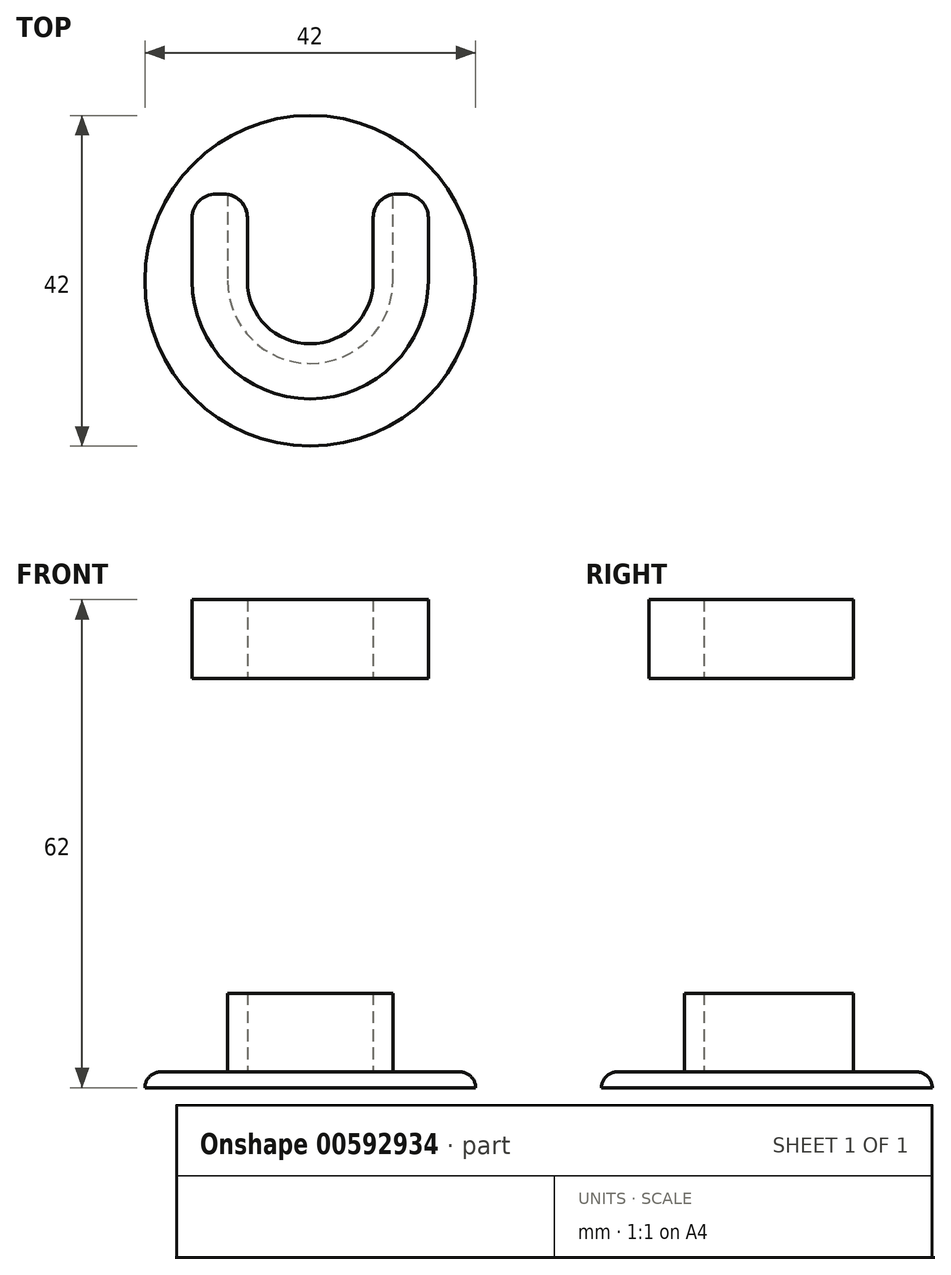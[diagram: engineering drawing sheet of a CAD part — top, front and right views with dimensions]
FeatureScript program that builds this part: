
annotation { "Feature Type Name" : "Feature", "Feature Type Description" : "" }
export const myFeature = defineFeature(function(context is Context, id is Id, definition is map)
    precondition{}
    {
        {
            var Q0;
            Q0=qCreatedBy(makeId("Top.planeOp"),FACE);
            var sketch = newSketch(context, id + "F0", { "sketchPlane" : qUnion([Q0])});
            skCircle(sketch, "E0", {"center": v(0, 0) * mm, "radius": 21 * mm});
            skCircle(sketch, "E1", {"center": v(0, 0) * mm, "radius": 8 * mm});
            skCircle(sketch, "E2", {"center": v(0, 0) * mm, "radius": 10.5 * mm});
            skLineSegment(sketch, "E3", {"start": v(-10.5, 11) * mm, "end": v(-10.5, 0) * mm});
            skLineSegment(sketch, "E4", {"start": v(-17.89, 11) * mm, "end": v(17.89, 11) * mm});
            skLineSegment(sketch, "E5", {"start": v(-8, 0) * mm, "end": v(-8, 11) * mm});
            skLineSegment(sketch, "E6", {"start": v(8, 0) * mm, "end": v(8, 11) * mm});
            skLineSegment(sketch, "E7", {"start": v(10.5, 0) * mm, "end": v(10.5, 11) * mm});
            skSolve(sketch);
        }
        {
            var Q0;
            Q0=qSketchRegion(id+"F0",true);
            var Q1;
            Q1=makeQuery(id+"F0.imprint","IMPRINT",FACE,{"disambiguationData":[TD([[makeQuery(id+"F0.imprint","IMPRINT",EDGE,{"derivedFrom":sQuery(id+"F0.wireOp",EDGE,"E1")}),1.0]])]});
            var Q2;
            Q2=makeQuery(id+"F0.imprint","IMPRINT",FACE,{"disambiguationData":[TD([[makeQuery(id+"F0.imprint","IMPRINT",EDGE,{"derivedFrom":sQuery(id+"F0.wireOp",EDGE,"E1")}),-1.0]])]});
            var Q3;
            {var subQ0=sQuery(id+"F0.wireOp",EDGE,"E2");var subQ1=makeQuery(id+"F0.imprint","IMPRINT",VERTEX,{"disambiguationData":[OD(0.0)],"derivedFrom":subQ0});Q3=makeQuery(id+"F0.imprint","IMPRINT",FACE,{"disambiguationData":[TD([[makeQuery(id+"F0.imprint","IMPRINT",EDGE,{"disambiguationData":[TD([[subQ1,-1.0]])],"derivedFrom":subQ0}),1.0]])]});}
            var Q4;
            {var subQ0=sQuery(id+"F0.wireOp",EDGE,"E3");Q4=makeQuery(id+"F0.imprint","IMPRINT",FACE,{"disambiguationData":[TD([[makeQuery(id+"F0.imprint","IMPRINT",EDGE,{"derivedFrom":subQ0}),1.0]])]});}
            var Q5;
            {var subQ0=sQuery(id+"F0.wireOp",EDGE,"E6");var subQ1=sQuery(id+"F0.wireOp",EDGE,"E2");var subQ2=makeQuery(id+"F0.imprint","INTERSECT",VERTEX,{"derivedFrom":[subQ1,subQ0]});Q5=makeQuery(id+"F0.imprint","IMPRINT",FACE,{"disambiguationData":[TD([[makeQuery(id+"F0.imprint","IMPRINT",EDGE,{"disambiguationData":[TD([[subQ2,-1.0]])],"derivedFrom":subQ1}),-1.0]])]});}
            var Q6;
            {var subQ0=sQuery(id+"F0.wireOp",EDGE,"E7");Q6=makeQuery(id+"F0.imprint","IMPRINT",FACE,{"disambiguationData":[TD([[makeQuery(id+"F0.imprint","IMPRINT",EDGE,{"derivedFrom":subQ0}),1.0]])]});}
            var Q7;
            {var subQ3=sQuery(id+"F0.wireOp",EDGE,"E5");var subQ7=sQuery(id+"F0.wireOp",EDGE,"E1");var subQ8=makeQuery(id+"F0.imprint","INTERSECT",VERTEX,{"derivedFrom":[subQ7,subQ3]});Q7=makeQuery(id+"F0.imprint","IMPRINT",FACE,{"disambiguationData":[TD([[makeQuery(id+"F0.imprint","IMPRINT",EDGE,{"disambiguationData":[TD([[subQ8,-1.0]])],"derivedFrom":subQ7}),-1.0]])]});}
            extrude(context, id + "F1", {"entities" : qUnion([Q0, Q1, Q2, Q3, Q4, Q5, Q6, Q7]), "oppositeDirection" : true, "depth" : 2 * mm, "offsetDistance" : 25 * mm});
        }
        {
            var Q0;
            {var subQ0=sQuery(id+"F0.wireOp",EDGE,"E7");Q0=makeQuery(id+"F0.imprint","IMPRINT",FACE,{"disambiguationData":[TD([[makeQuery(id+"F0.imprint","IMPRINT",EDGE,{"derivedFrom":subQ0}),1.0]])]});}
            var Q1;
            {var subQ3=sQuery(id+"F0.wireOp",EDGE,"E5");var subQ7=sQuery(id+"F0.wireOp",EDGE,"E1");var subQ8=makeQuery(id+"F0.imprint","INTERSECT",VERTEX,{"derivedFrom":[subQ7,subQ3]});Q1=makeQuery(id+"F0.imprint","IMPRINT",FACE,{"disambiguationData":[TD([[makeQuery(id+"F0.imprint","IMPRINT",EDGE,{"disambiguationData":[TD([[subQ8,-1.0]])],"derivedFrom":subQ7}),-1.0]])]});}
            var Q2;
            {var subQ0=sQuery(id+"F0.wireOp",EDGE,"E3");Q2=makeQuery(id+"F0.imprint","IMPRINT",FACE,{"disambiguationData":[TD([[makeQuery(id+"F0.imprint","IMPRINT",EDGE,{"derivedFrom":subQ0}),1.0]])]});}
            extrude(context, id + "F2", {"entities" : qUnion([Q0, Q1, Q2]), "operationType" : NewBodyOperationType.ADD, "depth" : 10 * mm, "offsetDistance" : 25 * mm});
        }
        {
            var Q0;
            Q0=makeQuery(id+"F1.opExtrude","CAP_EDGE",EDGE,{"disambiguationData":[OSD([sQuery(id+"F0.wireOp",EDGE,"E0")])],"isStart":true});
            var Q1;
            Q1=makeQuery(id+"F2.opExtrude","CAP_EDGE",EDGE,{"disambiguationData":[OSD([sQuery(id+"F0.wireOp",EDGE,"E2")])],"isStart":true});
            fillet(context, id + "F3", {"entities" : qUnion([Q0, Q1]), "radius" : 2 * mm, "tangentPropagation" : true, "allowEdgeOverflow" : false});
        }
        {
            var Q0;
            Q0=makeQuery(id+"F2.opExtrude","SWEPT_EDGE",EDGE,{"disambiguationData":[OSD([sQuery(id+"F0.wireOp",EDGE,"E4"),sQuery(id+"F0.wireOp",EDGE,"E5")])]});
            var Q1;
            Q1=makeQuery(id+"F2.opExtrude","SWEPT_EDGE",EDGE,{"disambiguationData":[OSD([sQuery(id+"F0.wireOp",EDGE,"E4"),sQuery(id+"F0.wireOp",EDGE,"E6")])]});
            fillet(context, id + "F4", {"entities" : qUnion([Q0, Q1]), "radius" : 3 * mm, "tangentPropagation" : true, "allowEdgeOverflow" : false});
        }
        {
            var Q0;
            Q0=qCreatedBy(makeId("Top.planeOp"),FACE);
            cPlane(context, id + "F5", {"entities" : qUnion([Q0]), "cplaneType" : CPlaneType.OFFSET, "offset" : 50 * mm, "width" : 150 * mm, "height" : 150 * mm});
        }
        {
            var Q0;
            Q0=qCreatedBy(id+"F5.planeOp",FACE);
            var sketch = newSketch(context, id + "F6", { "sketchPlane" : qUnion([Q0])});
            skCircle(sketch, "E8", {"center": v(0, 0) * mm, "radius": 15 * mm});
            skCircle(sketch, "E9", {"center": v(0, 0) * mm, "radius": 8 * mm});
            skLineSegment(sketch, "E10", {"start": v(-15, 0) * mm, "end": v(-15, 11) * mm});
            skLineSegment(sketch, "E11", {"start": v(-8, 0) * mm, "end": v(-8, 11) * mm});
            skLineSegment(sketch, "E12", {"start": v(8, 0) * mm, "end": v(8, 11) * mm});
            skLineSegment(sketch, "E13", {"start": v(15, 0) * mm, "end": v(15, 11) * mm});
            skLineSegment(sketch, "E14", {"start": v(15, 11) * mm, "end": v(8, 11) * mm});
            skLineSegment(sketch, "E15", {"start": v(-15, 11) * mm, "end": v(-8, 11) * mm});
            skSolve(sketch);
        }
        {
            var Q0;
            {var subQ0=sQuery(id+"F6.wireOp",EDGE,"E10");Q0=makeQuery(id+"F6.imprint","IMPRINT",FACE,{"disambiguationData":[TD([[makeQuery(id+"F6.imprint","IMPRINT",EDGE,{"derivedFrom":subQ0}),-1.0]])]});}
            var Q1;
            {var subQ0=sQuery(id+"F6.wireOp",EDGE,"E8");var subQ2=makeQuery(id+"F6.imprint","INTERSECT",VERTEX,{"derivedFrom":[subQ0,sQuery(id+"F6.wireOp",EDGE,"E13")]});Q1=makeQuery(id+"F6.imprint","IMPRINT",FACE,{"disambiguationData":[TD([[makeQuery(id+"F6.imprint","IMPRINT",EDGE,{"disambiguationData":[TD([[subQ2,-1.0]])],"derivedFrom":subQ0}),1.0]])]});}
            var Q2;
            {var subQ0=sQuery(id+"F6.wireOp",EDGE,"E13");Q2=makeQuery(id+"F6.imprint","IMPRINT",FACE,{"disambiguationData":[TD([[makeQuery(id+"F6.imprint","IMPRINT",EDGE,{"derivedFrom":subQ0}),1.0]])]});}
            extrude(context, id + "F7", {"entities" : qUnion([Q0, Q1, Q2]), "depth" : 10 * mm, "offsetDistance" : 25 * mm});
        }
        {
            var Q0;
            Q0=makeQuery(id+"F7.opExtrude","SWEPT_EDGE",EDGE,{"disambiguationData":[OSD([sQuery(id+"F6.wireOp",EDGE,"E11"),sQuery(id+"F6.wireOp",EDGE,"E15")])]});
            var Q1;
            Q1=makeQuery(id+"F7.opExtrude","SWEPT_EDGE",EDGE,{"disambiguationData":[OSD([sQuery(id+"F6.wireOp",EDGE,"E12"),sQuery(id+"F6.wireOp",EDGE,"E14")])]});
            var Q2;
            Q2=makeQuery(id+"F7.opExtrude","SWEPT_EDGE",EDGE,{"disambiguationData":[OSD([sQuery(id+"F6.wireOp",EDGE,"E10"),sQuery(id+"F6.wireOp",EDGE,"E15")])]});
            var Q3;
            Q3=makeQuery(id+"F7.opExtrude","SWEPT_EDGE",EDGE,{"disambiguationData":[OSD([sQuery(id+"F6.wireOp",EDGE,"E13"),sQuery(id+"F6.wireOp",EDGE,"E14")])]});
            fillet(context, id + "F8", {"entities" : qUnion([Q0, Q1, Q2, Q3]), "radius" : 3 * mm, "tangentPropagation" : true, "allowEdgeOverflow" : false});
        }
    });
